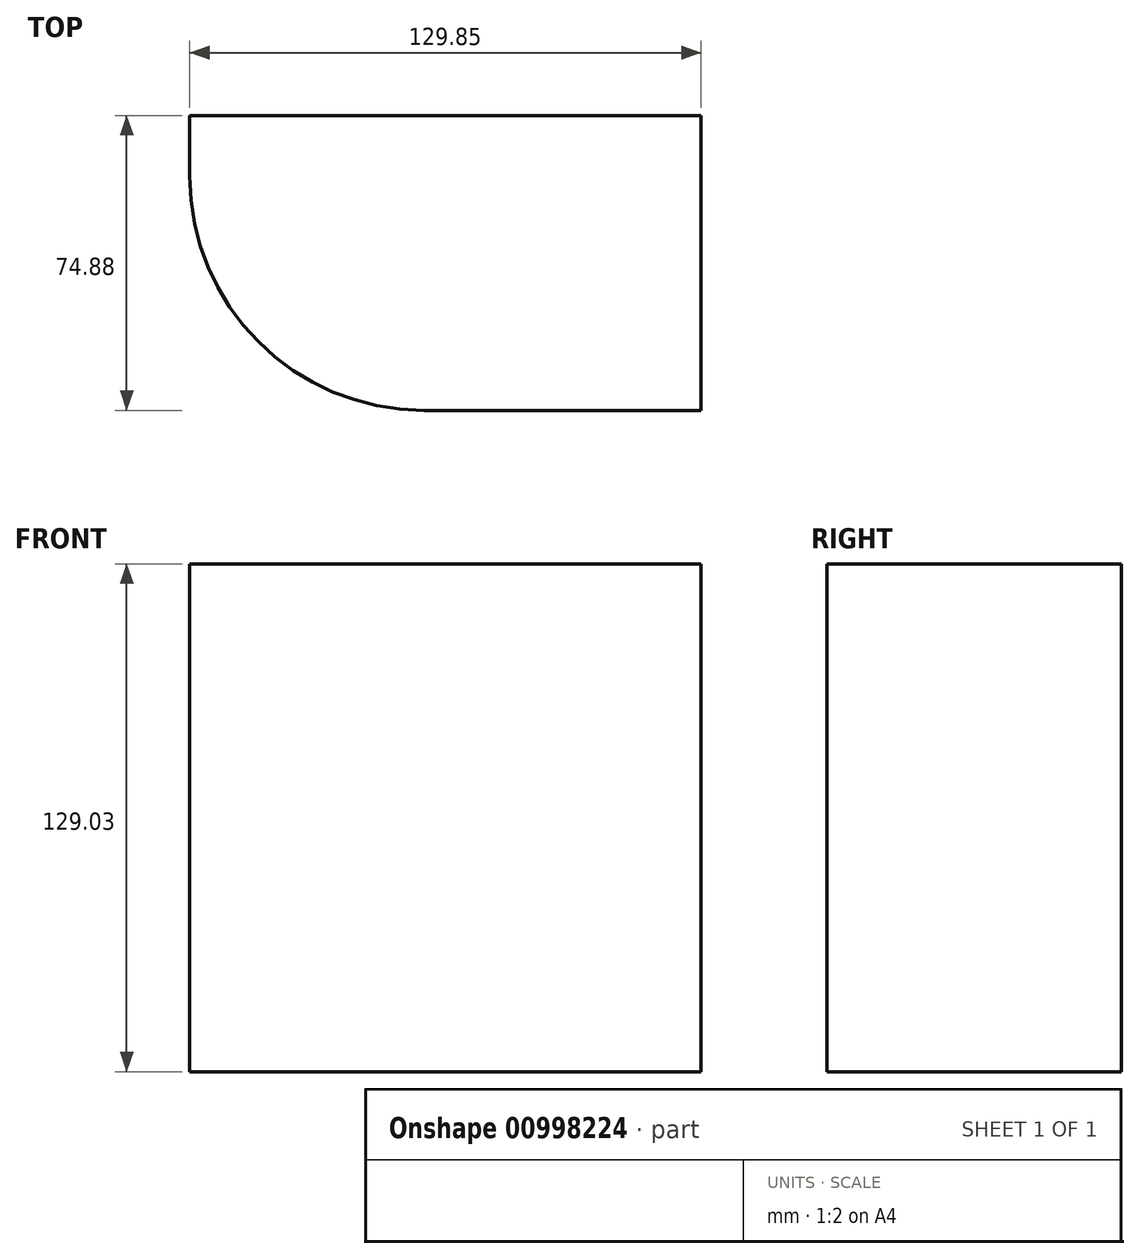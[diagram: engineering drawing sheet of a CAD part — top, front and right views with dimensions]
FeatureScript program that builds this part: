
annotation { "Feature Type Name" : "Feature", "Feature Type Description" : "" }
export const myFeature = defineFeature(function(context is Context, id is Id, definition is map)
    precondition{}
    {
        {
            var Q0;
            Q0=qCreatedBy(makeId("Top.planeOp"),FACE);
            var sketch = newSketch(context, id + "F0", { "sketchPlane" : qUnion([Q0])});
            skLineSegment(sketch, "E0.bottom", {"start": v(-62.92, -6.58) * mm, "end": v(66.93, -6.58) * mm});
            skLineSegment(sketch, "E0.top", {"start": v(-62.92, -81.46) * mm, "end": v(66.93, -81.46) * mm});
            skLineSegment(sketch, "E0.left", {"start": v(-62.92, -6.58) * mm, "end": v(-62.92, -81.46) * mm});
            skLineSegment(sketch, "E0.right", {"start": v(66.93, -6.58) * mm, "end": v(66.93, -81.46) * mm});
            skSolve(sketch);
        }
        {
            var Q0;
            Q0=makeQuery(id+"F0.imprint","IMPRINT",FACE,{"disambiguationData":[TD([[makeQuery(id+"F0.imprint","IMPRINT",EDGE,{"derivedFrom":sQuery(id+"F0.wireOp",EDGE,"E0.bottom")}),-1.0]])]});
            extrude(context, id + "F1", {"entities" : qUnion([Q0]), "depth" : 129.03 * mm, "offsetDistance" : 25.4 * mm});
        }
        {
            var Q0;
            Q0=makeQuery(id+"F1.opExtrude","SWEPT_EDGE",EDGE,{"disambiguationData":[OSD([sQuery(id+"F0.wireOp",EDGE,"E0.top"),sQuery(id+"F0.wireOp",EDGE,"E0.left")])]});
            fillet(context, id + "F2", {"entities" : qUnion([Q0]), "radius" : 59.48 * mm, "tangentPropagation" : true, "allowEdgeOverflow" : false});
        }
    });
